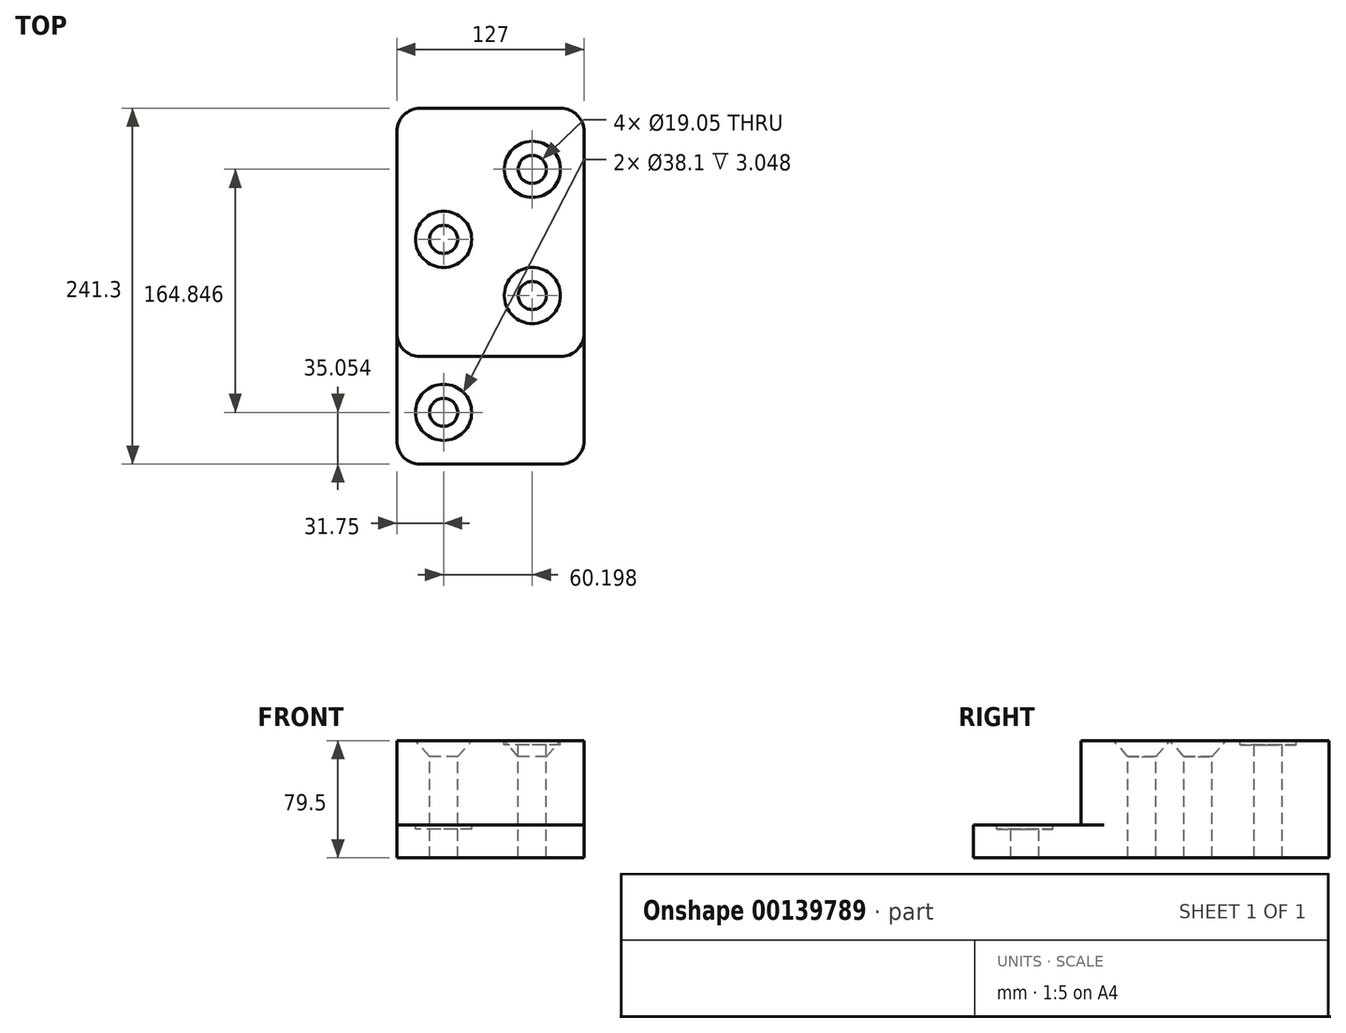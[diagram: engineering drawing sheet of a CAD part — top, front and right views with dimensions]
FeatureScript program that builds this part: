
annotation { "Feature Type Name" : "Feature", "Feature Type Description" : "" }
export const myFeature = defineFeature(function(context is Context, id is Id, definition is map)
    precondition{}
    {
        {
            var Q0;
            Q0=qCreatedBy(makeId("Top.planeOp"),FACE);
            var sketch = newSketch(context, id + "F0", { "sketchPlane" : qUnion([Q0])});
            skLineSegment(sketch, "E0.bottom", {"start": v(-63.5, 0) * mm, "end": v(63.5, 0) * mm});
            skLineSegment(sketch, "E0.top", {"start": v(-63.5, 168.4) * mm, "end": v(63.5, 168.4) * mm});
            skLineSegment(sketch, "E0.left", {"start": v(-63.5, 0) * mm, "end": v(-63.5, 168.4) * mm});
            skLineSegment(sketch, "E0.right", {"start": v(63.5, 0) * mm, "end": v(63.5, 168.4) * mm});
            skLineSegment(sketch, "E1.top", {"start": v(-63.5, -72.9) * mm, "end": v(63.5, -72.9) * mm});
            skLineSegment(sketch, "E1.left", {"start": v(-63.5, 0) * mm, "end": v(-63.5, -72.9) * mm});
            skLineSegment(sketch, "E1.right", {"start": v(63.5, 0) * mm, "end": v(63.5, -72.9) * mm});
            skSolve(sketch);
        }
        {
            var Q0;
            Q0=makeQuery(id+"F0.imprint","IMPRINT",FACE,{"disambiguationData":[TD([[makeQuery(id+"F0.imprint","IMPRINT",EDGE,{"derivedFrom":sQuery(id+"F0.wireOp",EDGE,"E0.top")}),-1.0]])]});
            extrude(context, id + "F1", {"entities" : qUnion([Q0]), "depth" : 79.5 * mm});
        }
        {
            var Q0;
            Q0=makeQuery(id+"F0.imprint","IMPRINT",FACE,{"disambiguationData":[TD([[makeQuery(id+"F0.imprint","IMPRINT",EDGE,{"derivedFrom":sQuery(id+"F0.wireOp",EDGE,"E0.bottom")}),-1.0]])]});
            extrude(context, id + "F2", {"entities" : qUnion([Q0]), "operationType" : NewBodyOperationType.ADD, "depth" : 22.35 * mm});
        }
        {
            var Q0;
            Q0=makeQuery(id+"F1.opExtrude","CAP_FACE",FACE,{"disambiguationData":[OSD([sQuery(id+"F0.wireOp",EDGE,"E0.top"),sQuery(id+"F0.wireOp",EDGE,"E0.left"),sQuery(id+"F0.wireOp",EDGE,"E0.right"),sQuery(id+"F0.wireOp",EDGE,"E0.bottom")])],"isStart":false});
            var sketch = newSketch(context, id + "F3", { "sketchPlane" : qUnion([Q0])});
            skPoint(sketch, "E2", {"position": v(28.45, 127) * mm});
            skPoint(sketch, "E3", {"position": v(-31.75, 79.5) * mm});
            skPoint(sketch, "E4", {"position": v(28.45, 41.4) * mm});
            skPoint(sketch, "E5", {"position": v(-31.75, -37.85) * mm});
            skSolve(sketch);
        }
        {
            var Q0;
            Q0=sQuery(id+"F3.wireOp",VERTEX,"E2");
            var Q1;
            Q1=sQuery(id+"F3.wireOp",VERTEX,"E5");
            var Q2;
            Q2=makeQuery(id+"F1.opExtrude","SWEPT_BODY",BODY,{"disambiguationData":[OSD([sQuery(id+"F0.wireOp",EDGE,"E0.top"),sQuery(id+"F0.wireOp",EDGE,"E0.left"),sQuery(id+"F0.wireOp",EDGE,"E0.right"),sQuery(id+"F0.wireOp",EDGE,"E0.bottom")])]});
            hole(context, id + "F4", {"style" : HoleStyle.C_BORE, "endStyle" : HoleEndStyle.THROUGH, "holeDiameter" : 19.05 * mm, "cBoreDiameter" : 38.1 * mm, "cBoreDepth" : 3.05 * mm, "locations" : qUnion([Q0, Q1]), "scope" : qUnion([Q2]), "isTappedThrough" : true});
        }
        {
            var Q0;
            Q0=sQuery(id+"F3.wireOp",VERTEX,"E3");
            var Q1;
            Q1=sQuery(id+"F3.wireOp",VERTEX,"E4");
            var Q2;
            Q2=makeQuery(id+"F1.opExtrude","SWEPT_BODY",BODY,{"disambiguationData":[OSD([sQuery(id+"F0.wireOp",EDGE,"E0.top"),sQuery(id+"F0.wireOp",EDGE,"E0.left"),sQuery(id+"F0.wireOp",EDGE,"E0.right"),sQuery(id+"F0.wireOp",EDGE,"E0.bottom")])]});
            hole(context, id + "F5", {"style" : HoleStyle.C_SINK, "endStyle" : HoleEndStyle.THROUGH, "holeDiameter" : 19.05 * mm, "cSinkDiameter" : 38.1 * mm, "cSinkAngle" : 82 * degree, "locations" : qUnion([Q0, Q1]), "scope" : qUnion([Q2]), "isTappedThrough" : true});
        }
        {
            var Q0;
            Q0=makeQuery(id+"F2.opExtrude","SWEPT_EDGE",EDGE,{"disambiguationData":[OSD([sQuery(id+"F0.wireOp",EDGE,"E1.top"),sQuery(id+"F0.wireOp",EDGE,"E1.right")])]});
            var Q1;
            Q1=makeQuery(id+"F2.opExtrude","SWEPT_EDGE",EDGE,{"disambiguationData":[OSD([sQuery(id+"F0.wireOp",EDGE,"E1.top"),sQuery(id+"F0.wireOp",EDGE,"E1.left")])]});
            var Q2;
            Q2=makeQuery(id+"F1.opExtrude","SWEPT_EDGE",EDGE,{"disambiguationData":[OSD([sQuery(id+"F0.wireOp",EDGE,"E0.right"),sQuery(id+"F0.wireOp",EDGE,"E0.bottom"),sQuery(id+"F0.wireOp",EDGE,"E1.right")])]});
            var Q3;
            Q3=makeQuery(id+"F1.opExtrude","SWEPT_EDGE",EDGE,{"disambiguationData":[OSD([sQuery(id+"F0.wireOp",EDGE,"E0.left"),sQuery(id+"F0.wireOp",EDGE,"E0.bottom"),sQuery(id+"F0.wireOp",EDGE,"E1.left")])]});
            var Q4;
            Q4=makeQuery(id+"F1.opExtrude","SWEPT_EDGE",EDGE,{"disambiguationData":[OSD([sQuery(id+"F0.wireOp",EDGE,"E0.top"),sQuery(id+"F0.wireOp",EDGE,"E0.right")])]});
            var Q5;
            Q5=makeQuery(id+"F1.opExtrude","SWEPT_EDGE",EDGE,{"disambiguationData":[OSD([sQuery(id+"F0.wireOp",EDGE,"E0.top"),sQuery(id+"F0.wireOp",EDGE,"E0.left")])]});
            fillet(context, id + "F6", {"entities" : qUnion([Q0, Q1, Q2, Q3, Q4, Q5]), "radius" : 15.75 * mm, "tangentPropagation" : true, "allowEdgeOverflow" : false});
        }
    });
